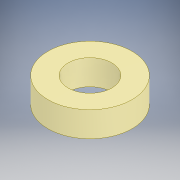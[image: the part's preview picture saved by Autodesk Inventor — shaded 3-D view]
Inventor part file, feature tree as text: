
AUTODESK INVENTOR PART (.ipt)
format: ipt  version: 2019 (Build 230136000, 136)  size: 98,304 bytes
history: native  units: mm
features: extrude x1, other x1
ambient origin geometry x8: Origin, YZ Plane, XZ Plane, XY Plane, X Axis, Y Axis, Z Axis, Center Point
bodies: Solid1 (feature_tree)
feature tree (2):
  extrude  "Washer"  Depth=10.0mm
  other  "Washer Cross Section"
